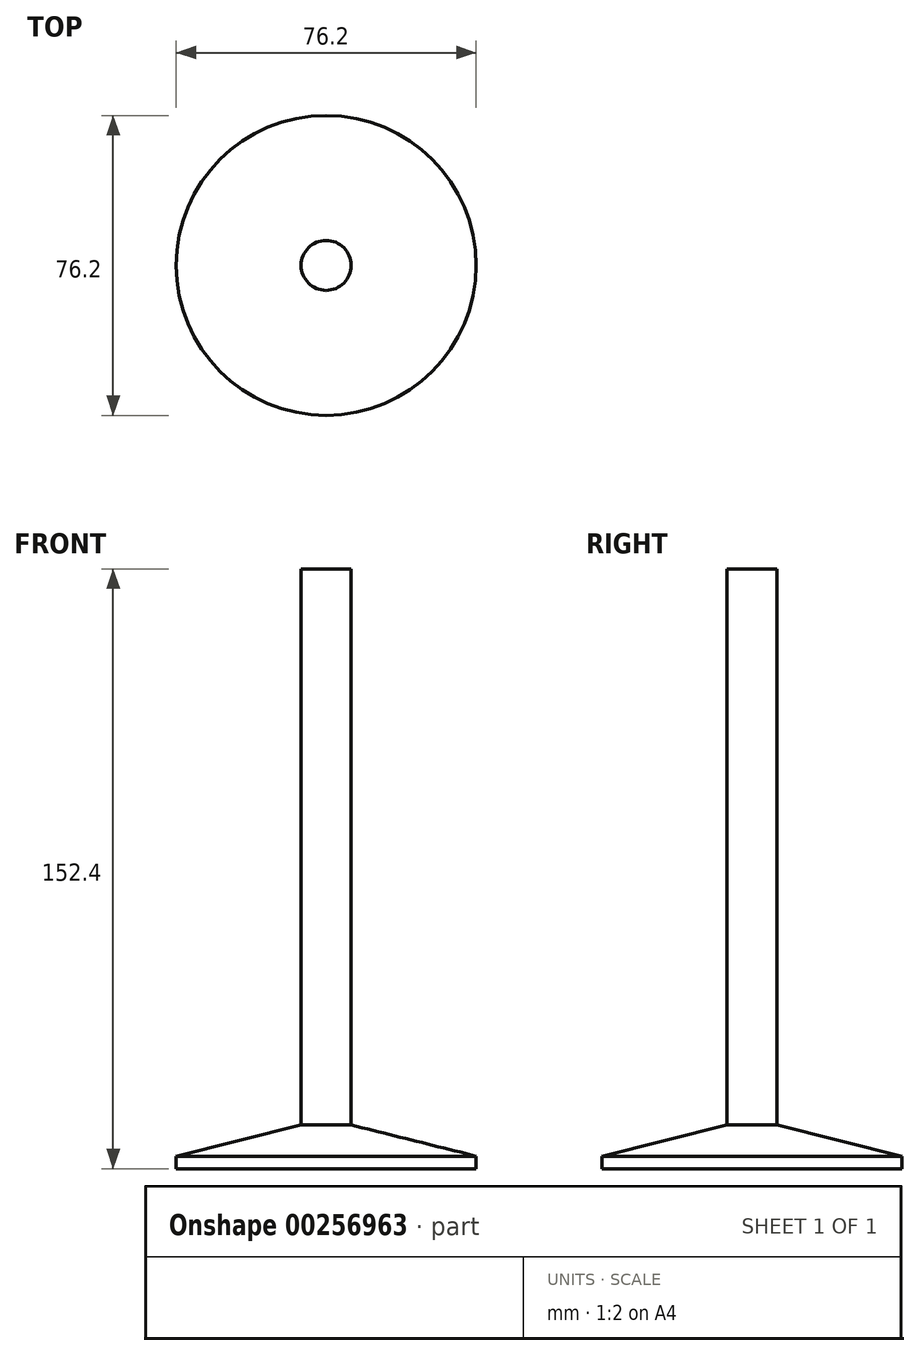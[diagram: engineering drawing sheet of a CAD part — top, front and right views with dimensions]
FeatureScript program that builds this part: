
annotation { "Feature Type Name" : "Feature", "Feature Type Description" : "" }
export const myFeature = defineFeature(function(context is Context, id is Id, definition is map)
    precondition{}
    {
        {
            var Q0;
            Q0=qCreatedBy(makeId("Front.planeOp"),FACE);
            var sketch = newSketch(context, id + "F0", { "sketchPlane" : qUnion([Q0])});
            skLineSegment(sketch, "E0", {"start": v(0, 98.54) * mm, "end": v(0, -84.8) * mm, "construction": true});
            skLineSegment(sketch, "E1", {"start": v(0, 0) * mm, "end": v(-38.1, 0) * mm});
            skLineSegment(sketch, "E2", {"start": v(-38.1, 0) * mm, "end": v(-38.1, 3.17) * mm});
            skLineSegment(sketch, "E3", {"start": v(-38.1, 3.17) * mm, "end": v(-6.35, 11.11) * mm});
            skLineSegment(sketch, "E4", {"start": v(-6.35, 11.11) * mm, "end": v(-6.35, 152.4) * mm});
            skLineSegment(sketch, "E5", {"start": v(-6.35, 152.4) * mm, "end": v(0, 152.4) * mm});
            skLineSegment(sketch, "E6", {"start": v(0, 152.4) * mm, "end": v(0, 0) * mm});
            skSolve(sketch);
        }
        {
            var Q0;
            Q0=makeQuery(id+"F0.imprint","IMPRINT",FACE,{"disambiguationData":[TD([[makeQuery(id+"F0.imprint","IMPRINT",EDGE,{"derivedFrom":sQuery(id+"F0.wireOp",EDGE,"E1")}),-1.0]])]});
            var Q1;
            Q1=sQuery(id+"F0.wireOp",EDGE,"E0");
            revolve(context, id + "F1", {"entities" : qUnion([Q0]), "axis" : qUnion([Q1]), "revolveType" : RevolveType.FULL});
        }
    });
